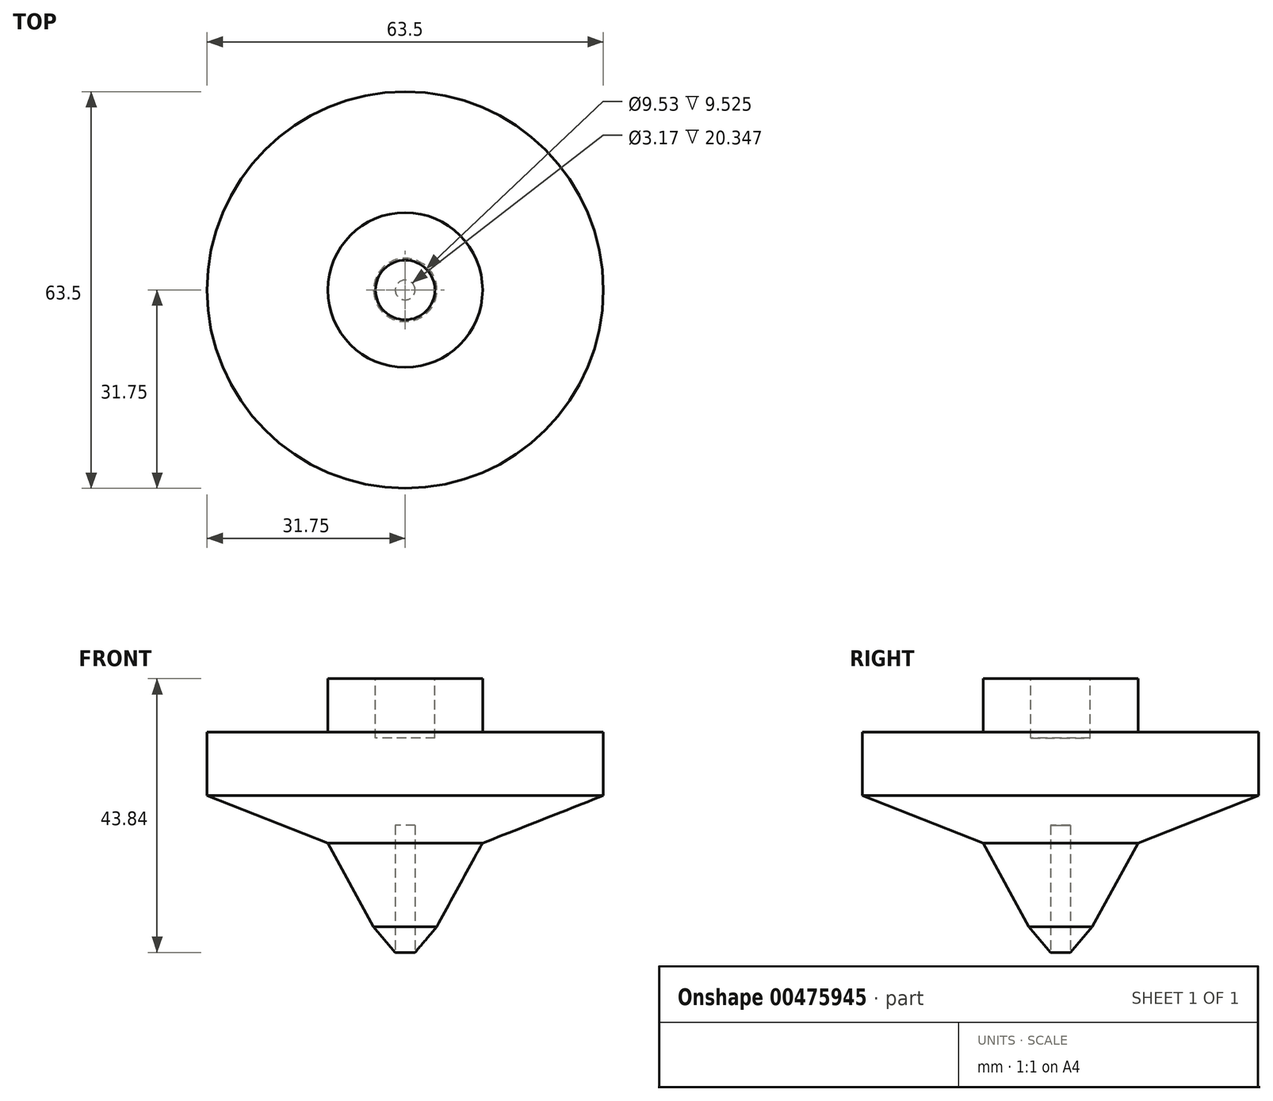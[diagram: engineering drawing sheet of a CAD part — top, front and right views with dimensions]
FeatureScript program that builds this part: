
annotation { "Feature Type Name" : "Feature", "Feature Type Description" : "" }
export const myFeature = defineFeature(function(context is Context, id is Id, definition is map)
    precondition{}
    {
        {
            var Q0;
            Q0=qCreatedBy(makeId("Front.planeOp"),FACE);
            var sketch = newSketch(context, id + "F0", { "sketchPlane" : qUnion([Q0])});
            skLineSegment(sketch, "E0", {"start": v(0, 0) * mm, "end": v(5.08, 6.01) * mm});
            skLineSegment(sketch, "E1", {"start": v(5.08, 6.01) * mm, "end": v(12.4, 19.38) * mm});
            skLineSegment(sketch, "E2", {"start": v(12.4, 19.38) * mm, "end": v(31.75, 27) * mm});
            skLineSegment(sketch, "E3", {"start": v(31.75, 27) * mm, "end": v(31.75, 37.16) * mm});
            skLineSegment(sketch, "E4", {"start": v(31.75, 37.16) * mm, "end": v(12.4, 37.16) * mm});
            skLineSegment(sketch, "E5", {"start": v(12.4, 37.16) * mm, "end": v(12.4, 45.72) * mm});
            skLineSegment(sketch, "E6", {"start": v(12.4, 45.72) * mm, "end": v(0, 45.72) * mm});
            skLineSegment(sketch, "E7", {"start": v(0, 45.72) * mm, "end": v(0, 0) * mm});
            skSolve(sketch);
        }
        {
            var Q0;
            Q0=makeQuery(id+"F0.imprint","IMPRINT",FACE,{"disambiguationData":[TD([[makeQuery(id+"F0.imprint","IMPRINT",EDGE,{"derivedFrom":sQuery(id+"F0.wireOp",EDGE,"E0")}),1.0]])]});
            var Q1;
            Q1=sQuery(id+"F0.wireOp",EDGE,"E7");
            revolve(context, id + "F1", {"entities" : qUnion([Q0]), "axis" : qUnion([Q1]), "revolveType" : RevolveType.FULL});
        }
        {
            var Q0;
            Q0=makeQuery(id+"F1.opRevolve","SWEPT_FACE",FACE,{"disambiguationData":[OSD([sQuery(id+"F0.wireOp",EDGE,"E6")])]});
            var sketch = newSketch(context, id + "F2", { "sketchPlane" : qUnion([Q0])});
            skCircle(sketch, "E8", {"center": v(0, 0) * mm, "radius": 4.76 * mm});
            skSolve(sketch);
        }
        {
            var Q0;
            Q0=makeQuery(id+"F2.imprint","IMPRINT",FACE,{"disambiguationData":[TD([[makeQuery(id+"F2.imprint","IMPRINT",EDGE,{"derivedFrom":sQuery(id+"F2.wireOp",EDGE,"E8")}),1.0]])]});
            extrude(context, id + "F3", {"entities" : qUnion([Q0]), "operationType" : NewBodyOperationType.REMOVE, "oppositeDirection" : true, "depth" : 9.52 * mm});
        }
        {
            var Q0;
            Q0=qCreatedBy(makeId("Top.planeOp"),FACE);
            var sketch = newSketch(context, id + "F4", { "sketchPlane" : qUnion([Q0])});
            skCircle(sketch, "E9", {"center": v(0, 0) * mm, "radius": 1.59 * mm});
            skSolve(sketch);
        }
        {
            var Q0;
            Q0 = qSketchRegion(id + "F4", true);
            extrude(context, id + "F5", {"entities" : qUnion([Q0]), "operationType" : NewBodyOperationType.REMOVE, "depth" : 22.22 * mm});
        }
    });
